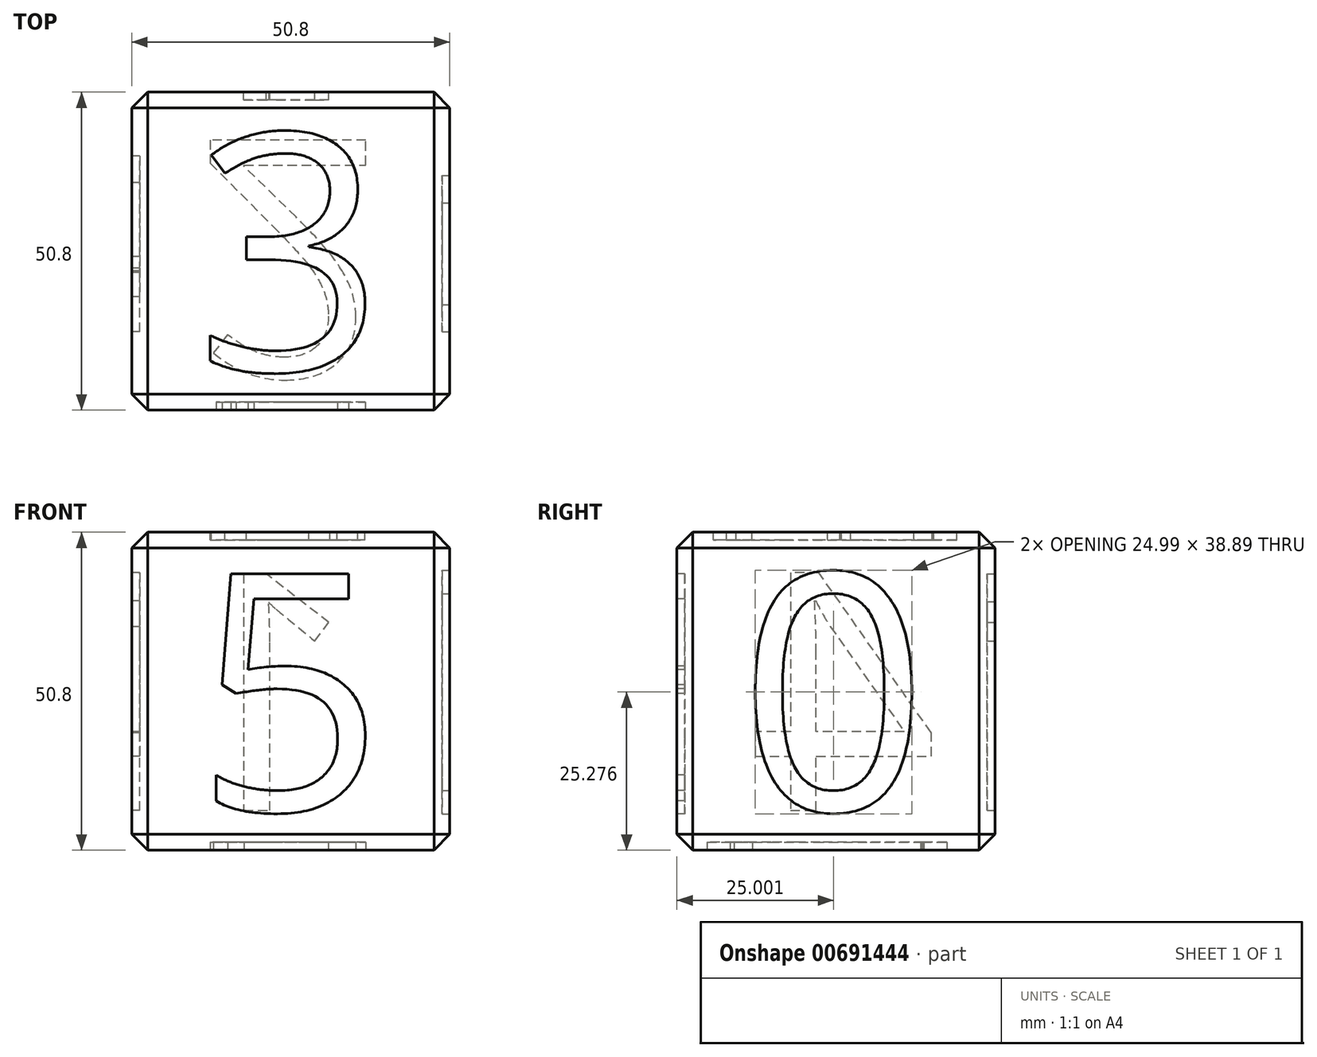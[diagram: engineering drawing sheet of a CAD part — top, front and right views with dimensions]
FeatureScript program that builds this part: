
annotation { "Feature Type Name" : "Feature", "Feature Type Description" : "" }
export const myFeature = defineFeature(function(context is Context, id is Id, definition is map)
    precondition{}
    {
        {
            var Q0;
            Q0=qCreatedBy(makeId("Top.planeOp"),FACE);
            var sketch = newSketch(context, id + "F0", { "sketchPlane" : qUnion([Q0])});
            skLineSegment(sketch, "E0.bottom", {"start": v(25.4, 25.4) * mm, "end": v(-25.4, 25.4) * mm});
            skLineSegment(sketch, "E0.top", {"start": v(25.4, -25.4) * mm, "end": v(-25.4, -25.4) * mm});
            skLineSegment(sketch, "E0.left", {"start": v(25.4, 25.4) * mm, "end": v(25.4, -25.4) * mm});
            skLineSegment(sketch, "E0.right", {"start": v(-25.4, 25.4) * mm, "end": v(-25.4, -25.4) * mm});
            skPoint(sketch, "E0.middle", {"position": v(0, 0) * mm});
            skSolve(sketch);
        }
        {
            var Q0;
            Q0 = qSketchRegion(id + "F0", true);
            extrude(context, id + "F1", {"entities" : qUnion([Q0]), "depth" : 25.4 * mm, "offsetDistance" : 25.4 * mm, "hasSecondDirection" : true, "secondDirectionOppositeDirection" : true, "secondDirectionDepth" : 25.4 * mm});
        }
        {
            var Q0;
            Q0=makeQuery(id+"F1.opExtrude","SWEPT_FACE",FACE,{"disambiguationData":[OSD([sQuery(id+"F0.wireOp",EDGE,"E0.right")])]});
            var Q1;
            Q1=makeQuery(id+"F1.opExtrude","CAP_FACE",FACE,{"disambiguationData":[OSD([sQuery(id+"F0.wireOp",EDGE,"E0.bottom"),sQuery(id+"F0.wireOp",EDGE,"E0.top"),sQuery(id+"F0.wireOp",EDGE,"E0.left"),sQuery(id+"F0.wireOp",EDGE,"E0.right")])],"isStart":false});
            var Q2;
            Q2=makeQuery(id+"F1.opExtrude","SWEPT_FACE",FACE,{"disambiguationData":[OSD([sQuery(id+"F0.wireOp",EDGE,"E0.bottom")])]});
            var Q3;
            Q3=makeQuery(id+"F1.opExtrude","SWEPT_FACE",FACE,{"disambiguationData":[OSD([sQuery(id+"F0.wireOp",EDGE,"E0.left")])]});
            var Q4;
            Q4=makeQuery(id+"F1.opExtrude","SWEPT_FACE",FACE,{"disambiguationData":[OSD([sQuery(id+"F0.wireOp",EDGE,"E0.top")])]});
            chamfer(context, id + "F2", {"entities" : qUnion([Q0, Q1, Q2, Q3, Q4]), "width" : 2.54 * mm, "tangentPropagation" : true});
        }
        {
            var Q0;
            Q0=makeQuery(id+"F1.opExtrude","SWEPT_FACE",FACE,{"disambiguationData":[OSD([sQuery(id+"F0.wireOp",EDGE,"E0.left")])]});
            var sketch = newSketch(context, id + "F3", { "sketchPlane" : qUnion([Q0])});
            skText(sketch, "E1", { "text": "0", "fontName": "OpenSans-Regular.ttf"});
            skLineSegment(sketch, "E2", {"start": v(-15.53, 0) * mm, "end": v(-38, 0) * mm, "construction": true});
            const initialGuessF3  = {"E1": [-0.01553, -0.01905, 1, 0, 0.0381]};
            skSetInitialGuess(sketch, initialGuessF3);
            skSolve(sketch);
        }
        {
            var Q0;
            Q0 = qSketchRegion(id + "F3", true);
            extrude(context, id + "F4", {"entities" : qUnion([Q0]), "operationType" : NewBodyOperationType.REMOVE, "oppositeDirection" : true, "depth" : 1.27 * mm, "offsetDistance" : 25.4 * mm});
        }
        {
            var Q0;
            Q0=makeQuery(id+"F1.opExtrude","SWEPT_FACE",FACE,{"disambiguationData":[OSD([sQuery(id+"F0.wireOp",EDGE,"E0.bottom")])]});
            var sketch = newSketch(context, id + "F5", { "sketchPlane" : qUnion([Q0])});
            skText(sketch, "E3", { "text": "1", "fontName": "OpenSans-Regular.ttf"});
            skLineSegment(sketch, "E4", {"start": v(-10.95, 0) * mm, "end": v(-31.36, 0) * mm, "construction": true});
            const initialGuessF5  = {"E3": [-0.01095, -0.01905, 1, 0, 0.0381]};
            skSetInitialGuess(sketch, initialGuessF5);
            skSolve(sketch);
        }
        {
            var Q0;
            Q0 = qSketchRegion(id + "F5", true);
            extrude(context, id + "F6", {"entities" : qUnion([Q0]), "operationType" : NewBodyOperationType.REMOVE, "oppositeDirection" : true, "depth" : 1.27 * mm, "offsetDistance" : 25.4 * mm});
        }
        {
            var Q0;
            Q0=makeQuery(id+"F1.opExtrude","CAP_FACE",FACE,{"disambiguationData":[OSD([sQuery(id+"F0.wireOp",EDGE,"E0.bottom"),sQuery(id+"F0.wireOp",EDGE,"E0.top"),sQuery(id+"F0.wireOp",EDGE,"E0.left"),sQuery(id+"F0.wireOp",EDGE,"E0.right")])],"isStart":true});
            var sketch = newSketch(context, id + "F7", { "sketchPlane" : qUnion([Q0])});
            skText(sketch, "E5", { "text": "2", "fontName": "OpenSans-Regular.ttf"});
            skLineSegment(sketch, "E6", {"start": v(-15.42, 1.33) * mm, "end": v(-37.06, 1.33) * mm, "construction": true});
            const initialGuessF7  = {"E5": [-0.01542, -0.01772, 1, 0, 0.0381]};
            skSetInitialGuess(sketch, initialGuessF7);
            skSolve(sketch);
        }
        {
            var Q0;
            Q0 = qSketchRegion(id + "F7", true);
            extrude(context, id + "F8", {"entities" : qUnion([Q0]), "operationType" : NewBodyOperationType.REMOVE, "oppositeDirection" : true, "depth" : 1.27 * mm, "offsetDistance" : 25.4 * mm});
        }
        {
            var Q0;
            Q0=makeQuery(id+"F1.opExtrude","CAP_FACE",FACE,{"disambiguationData":[OSD([sQuery(id+"F0.wireOp",EDGE,"E0.bottom"),sQuery(id+"F0.wireOp",EDGE,"E0.top"),sQuery(id+"F0.wireOp",EDGE,"E0.left"),sQuery(id+"F0.wireOp",EDGE,"E0.right")])],"isStart":false});
            var sketch = newSketch(context, id + "F9", { "sketchPlane" : qUnion([Q0])});
            skText(sketch, "E7", { "text": "3", "fontName": "OpenSans-Regular.ttf"});
            skLineSegment(sketch, "E8", {"start": v(-15.3, 0) * mm, "end": v(-30.23, 0) * mm, "construction": true});
            const initialGuessF9  = {"E7": [-0.0153, -0.01905, 1, 0, 0.0381]};
            skSetInitialGuess(sketch, initialGuessF9);
            skSolve(sketch);
        }
        {
            var Q0;
            Q0 = qSketchRegion(id + "F9", true);
            extrude(context, id + "F10", {"entities" : qUnion([Q0]), "operationType" : NewBodyOperationType.REMOVE, "oppositeDirection" : true, "depth" : 1.27 * mm, "offsetDistance" : 25.4 * mm});
        }
        {
            var Q0;
            Q0=makeQuery(id+"F1.opExtrude","SWEPT_FACE",FACE,{"disambiguationData":[OSD([sQuery(id+"F0.wireOp",EDGE,"E0.right")])]});
            var sketch = newSketch(context, id + "F11", { "sketchPlane" : qUnion([Q0])});
            skText(sketch, "E9", { "text": "4", "fontName": "OpenSans-Regular.ttf"});
            skLineSegment(sketch, "E10", {"start": v(-36.72, 0) * mm, "end": v(-16.31, 0) * mm, "construction": true});
            const initialGuessF11  = {"E9": [-0.01631, -0.01905, 1, 0, 0.0381]};
            skSetInitialGuess(sketch, initialGuessF11);
            skSolve(sketch);
        }
        {
            var Q0;
            Q0 = qSketchRegion(id + "F11", true);
            extrude(context, id + "F12", {"entities" : qUnion([Q0]), "operationType" : NewBodyOperationType.REMOVE, "oppositeDirection" : true, "depth" : 1.27 * mm, "offsetDistance" : 25.4 * mm});
        }
        {
            var Q0;
            Q0=makeQuery(id+"F1.opExtrude","SWEPT_FACE",FACE,{"disambiguationData":[OSD([sQuery(id+"F0.wireOp",EDGE,"E0.top")])]});
            var sketch = newSketch(context, id + "F13", { "sketchPlane" : qUnion([Q0])});
            skText(sketch, "E11", { "text": "5", "fontName": "OpenSans-Regular.ttf"});
            skLineSegment(sketch, "E12", {"start": v(-33.54, 0) * mm, "end": v(-15.32, 0) * mm, "construction": true});
            const initialGuessF13  = {"E11": [-0.01532, -0.01905, 1, 0, 0.0381]};
            skSetInitialGuess(sketch, initialGuessF13);
            skSolve(sketch);
        }
        {
            var Q0;
            Q0 = qSketchRegion(id + "F13", true);
            extrude(context, id + "F14", {"entities" : qUnion([Q0]), "operationType" : NewBodyOperationType.REMOVE, "oppositeDirection" : true, "depth" : 1.27 * mm, "offsetDistance" : 25.4 * mm});
        }
    });
